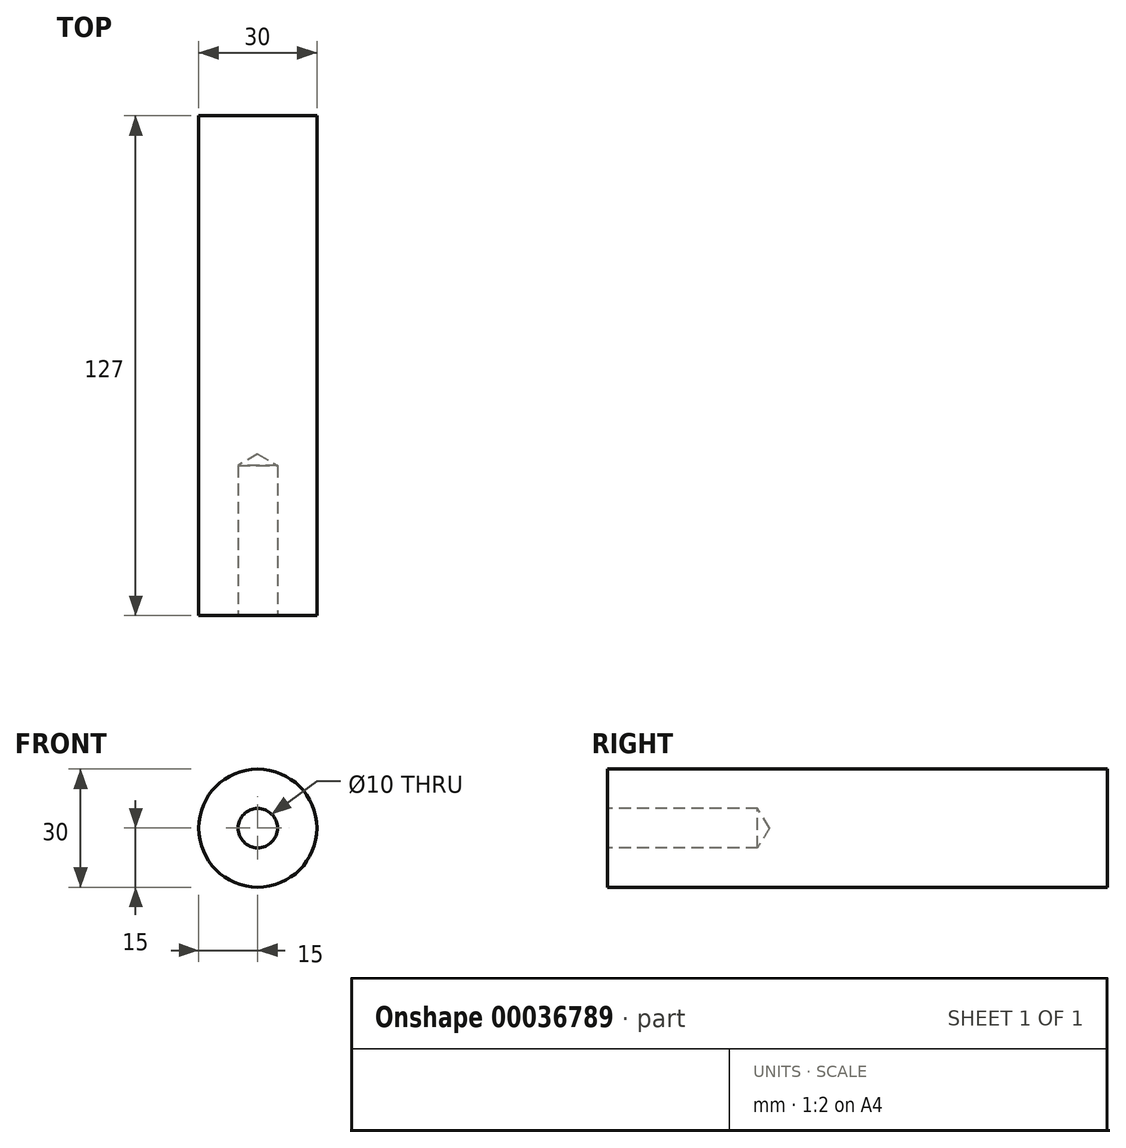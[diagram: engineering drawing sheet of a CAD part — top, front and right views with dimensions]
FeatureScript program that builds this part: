
annotation { "Feature Type Name" : "Feature", "Feature Type Description" : "" }
export const myFeature = defineFeature(function(context is Context, id is Id, definition is map)
    precondition{}
    {
        {
            var Q0;
            Q0=qCreatedBy(makeId("Front.planeOp"),FACE);
            var sketch = newSketch(context, id + "F0", { "sketchPlane" : qUnion([Q0])});
            skCircle(sketch, "E0", {"center": v(0, 0) * mm, "radius": 15 * mm});
            skSolve(sketch);
        }
        {
            var Q0;
            Q0=makeQuery(id+"F0.imprint","IMPRINT",FACE,{"disambiguationData":[TD([[makeQuery(id+"F0.imprint","IMPRINT",EDGE,{"derivedFrom":sQuery(id+"F0.wireOp",EDGE,"E0")}),1.0]])]});
            extrude(context, id + "F1", {"entities" : qUnion([Q0]), "depth" : 127 * mm});
        }
        {
            var Q0;
            Q0=makeQuery(id+"F1.opExtrude","CAP_FACE",FACE,{"disambiguationData":[OSD([sQuery(id+"F0.wireOp",EDGE,"E0")])],"isStart":false});
            var sketch = newSketch(context, id + "F2", { "sketchPlane" : qUnion([Q0])});
            skCircle(sketch, "E1.0.0", {"center": v(0, 0) * mm, "radius": 15 * mm, "construction": true});
            skSolve(sketch);
        }
        {
            var Q0;
            Q0=sQuery(id+"F2.wireOp",VERTEX,"E1.0.0.center");
            var Q1;
            Q1=makeQuery(id+"F1.opExtrude","SWEPT_BODY",BODY,{"disambiguationData":[OSD([sQuery(id+"F0.wireOp",EDGE,"E0")])]});
            hole(context, id + "F3", {"style" : HoleStyle.SIMPLE, "holeDiameter" : 10 * mm, "endStyle" : HoleEndStyle.BLIND, "holeDepth" : 38.1 * mm, "locations" : qUnion([Q0]), "scope" : qUnion([Q1])});
        }
    });
